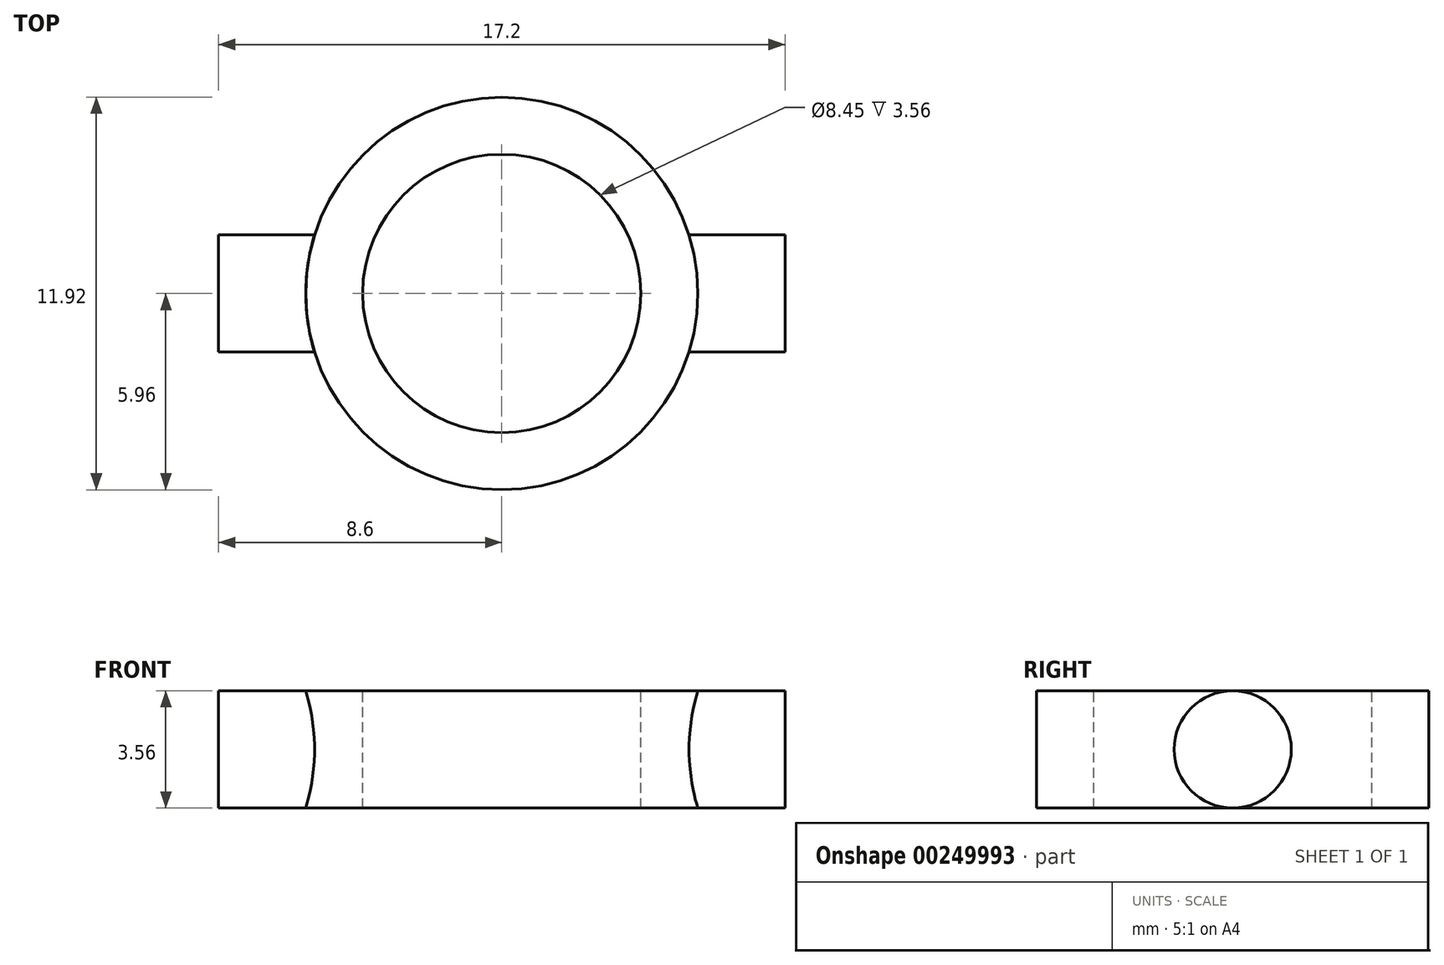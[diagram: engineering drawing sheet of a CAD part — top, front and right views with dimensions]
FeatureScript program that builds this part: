
annotation { "Feature Type Name" : "Feature", "Feature Type Description" : "" }
export const myFeature = defineFeature(function(context is Context, id is Id, definition is map)
    precondition{}
    {
        {
            var Q0;
            Q0=qCreatedBy(makeId("Right.planeOp"),FACE);
            var sketch = newSketch(context, id + "F0", { "sketchPlane" : qUnion([Q0])});
            skCircle(sketch, "E0", {"center": v(0, 1.78) * mm, "radius": 1.78 * mm});
            skSolve(sketch);
        }
        {
            var Q0;
            Q0 = qSketchRegion(id + "F0", true);
            extrude(context, id + "F1", {"entities" : qUnion([Q0]), "oppositeDirection" : true, "depth" : (17.2 / 2) * mm, "hasSecondDirection" : true, "secondDirectionOppositeDirection" : false, "secondDirectionDepth" : 8.6 * mm});
        }
        {
            var Q0;
            Q0=qCreatedBy(makeId("Top.planeOp"),FACE);
            var sketch = newSketch(context, id + "F2", { "sketchPlane" : qUnion([Q0])});
            skCircle(sketch, "E1", {"center": v(0, 0) * mm, "radius": 5.96 * mm});
            skSolve(sketch);
        }
        {
            var Q0;
            Q0 = qSketchRegion(id + "F2", true);
            extrude(context, id + "F3", {"entities" : qUnion([Q0]), "operationType" : NewBodyOperationType.ADD, "depth" : 3.56 * mm});
        }
        {
            var Q0;
            Q0=makeQuery(id+"F3.opExtrude","CAP_FACE",FACE,{"disambiguationData":[OSD([sQuery(id+"F2.wireOp",EDGE,"E1")])],"isStart":false});
            var sketch = newSketch(context, id + "F4", { "sketchPlane" : qUnion([Q0])});
            skCircle(sketch, "E2", {"center": v(0, 0) * mm, "radius": 4.22 * mm});
            skSolve(sketch);
        }
        {
            var Q0;
            Q0 = qSketchRegion(id + "F4", true);
            extrude(context, id + "F5", {"entities" : qUnion([Q0]), "operationType" : NewBodyOperationType.REMOVE, "oppositeDirection" : true, "depth" : 3.56 * mm});
        }
    });
